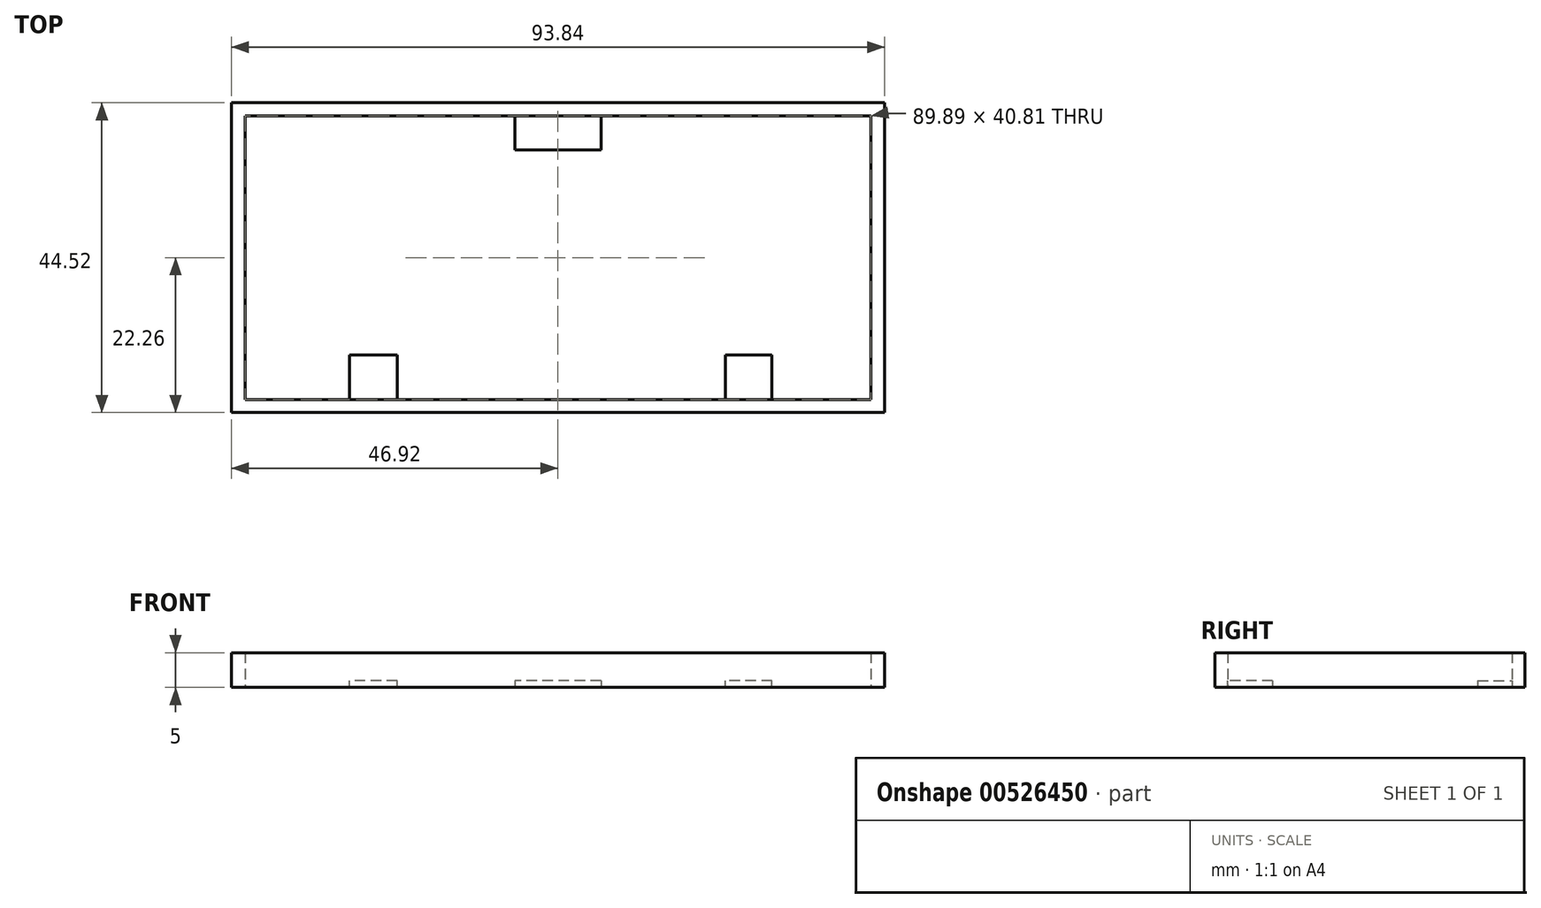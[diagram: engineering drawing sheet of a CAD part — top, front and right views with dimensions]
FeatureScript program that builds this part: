
annotation { "Feature Type Name" : "Feature", "Feature Type Description" : "" }
export const myFeature = defineFeature(function(context is Context, id is Id, definition is map)
    precondition{}
    {
        {
            var Q0;
            Q0=qCreatedBy(makeId("Top.planeOp"),FACE);
            var sketch = newSketch(context, id + "F0", { "sketchPlane" : qUnion([Q0])});
            skLineSegment(sketch, "E0.bottom", {"start": v(46.92, 22.26) * mm, "end": v(-46.92, 22.26) * mm});
            skLineSegment(sketch, "E0.top", {"start": v(46.92, -22.26) * mm, "end": v(-46.92, -22.26) * mm});
            skLineSegment(sketch, "E0.left", {"start": v(46.92, 22.26) * mm, "end": v(46.92, -22.26) * mm});
            skLineSegment(sketch, "E0.right", {"start": v(-46.92, 22.26) * mm, "end": v(-46.92, -22.26) * mm});
            skPoint(sketch, "E0.middle", {"position": v(0, 0) * mm});
            skLineSegment(sketch, "E1.bottom", {"start": v(44.94, -20.4) * mm, "end": v(-44.94, -20.4) * mm});
            skLineSegment(sketch, "E1.top", {"start": v(44.94, 20.4) * mm, "end": v(-44.94, 20.4) * mm});
            skLineSegment(sketch, "E1.left", {"start": v(44.94, -20.4) * mm, "end": v(44.94, 20.4) * mm});
            skLineSegment(sketch, "E1.right", {"start": v(-44.94, -20.4) * mm, "end": v(-44.94, 20.4) * mm});
            skSolve(sketch);
        }
        {
            var Q0;
            Q0=makeQuery(id+"F0.imprint","IMPRINT",FACE,{"disambiguationData":[TD([[makeQuery(id+"F0.imprint","IMPRINT",EDGE,{"derivedFrom":sQuery(id+"F0.wireOp",EDGE,"E0.bottom")}),1.0]])]});
            extrude(context, id + "F1", {"entities" : qUnion([Q0]), "depth" : 5 * mm, "offsetDistance" : 25.4 * mm});
        }
        {
            var Q0;
            Q0=qCreatedBy(makeId("Top.planeOp"),FACE);
            var sketch = newSketch(context, id + "F2", { "sketchPlane" : qUnion([Q0])});
            skLineSegment(sketch, "E2.bottom", {"start": v(6.18, 15.46) * mm, "end": v(-6.18, 15.46) * mm});
            skLineSegment(sketch, "E2.top", {"start": v(6.18, 21.98) * mm, "end": v(-6.18, 21.98) * mm});
            skLineSegment(sketch, "E2.left", {"start": v(6.18, 15.46) * mm, "end": v(6.18, 21.98) * mm});
            skLineSegment(sketch, "E2.right", {"start": v(-6.18, 15.46) * mm, "end": v(-6.18, 21.98) * mm});
            skPoint(sketch, "E2.middle", {"position": v(0, 18.72) * mm});
            skLineSegment(sketch, "E3.bottom", {"start": v(-23.1, -13.98) * mm, "end": v(-29.92, -13.98) * mm});
            skLineSegment(sketch, "E3.top", {"start": v(-23.1, -21.72) * mm, "end": v(-29.92, -21.72) * mm});
            skLineSegment(sketch, "E3.left", {"start": v(-23.1, -13.98) * mm, "end": v(-23.1, -21.72) * mm});
            skLineSegment(sketch, "E3.right", {"start": v(-29.92, -13.98) * mm, "end": v(-29.92, -21.72) * mm});
            skPoint(sketch, "E3.middle", {"position": v(-26.51, -17.85) * mm});
            skLineSegment(sketch, "E4.bottom", {"start": v(24.02, -13.98) * mm, "end": v(30.72, -13.98) * mm});
            skLineSegment(sketch, "E4.top", {"start": v(24.02, -21.51) * mm, "end": v(30.72, -21.51) * mm});
            skLineSegment(sketch, "E4.left", {"start": v(24.02, -13.98) * mm, "end": v(24.02, -21.51) * mm});
            skLineSegment(sketch, "E4.right", {"start": v(30.72, -13.98) * mm, "end": v(30.72, -21.51) * mm});
            skPoint(sketch, "E4.middle", {"position": v(27.37, -17.75) * mm});
            skSolve(sketch);
        }
        {
            var Q0;
            Q0=makeQuery(id+"F2.imprint","IMPRINT",FACE,{"disambiguationData":[TD([[makeQuery(id+"F2.imprint","IMPRINT",EDGE,{"derivedFrom":sQuery(id+"F2.wireOp",EDGE,"E2.bottom")}),-1.0]])]});
            var Q1;
            Q1=makeQuery(id+"F2.imprint","IMPRINT",FACE,{"disambiguationData":[TD([[makeQuery(id+"F2.imprint","IMPRINT",EDGE,{"derivedFrom":sQuery(id+"F2.wireOp",EDGE,"E3.bottom")}),1.0]])]});
            var Q2;
            Q2=makeQuery(id+"F2.imprint","IMPRINT",FACE,{"disambiguationData":[TD([[makeQuery(id+"F2.imprint","IMPRINT",EDGE,{"derivedFrom":sQuery(id+"F2.wireOp",EDGE,"E4.bottom")}),-1.0]])]});
            extrude(context, id + "F3", {"entities" : qUnion([Q0, Q1, Q2]), "operationType" : NewBodyOperationType.ADD, "depth" : 1 * mm, "offsetDistance" : 25.4 * mm});
        }
    });
